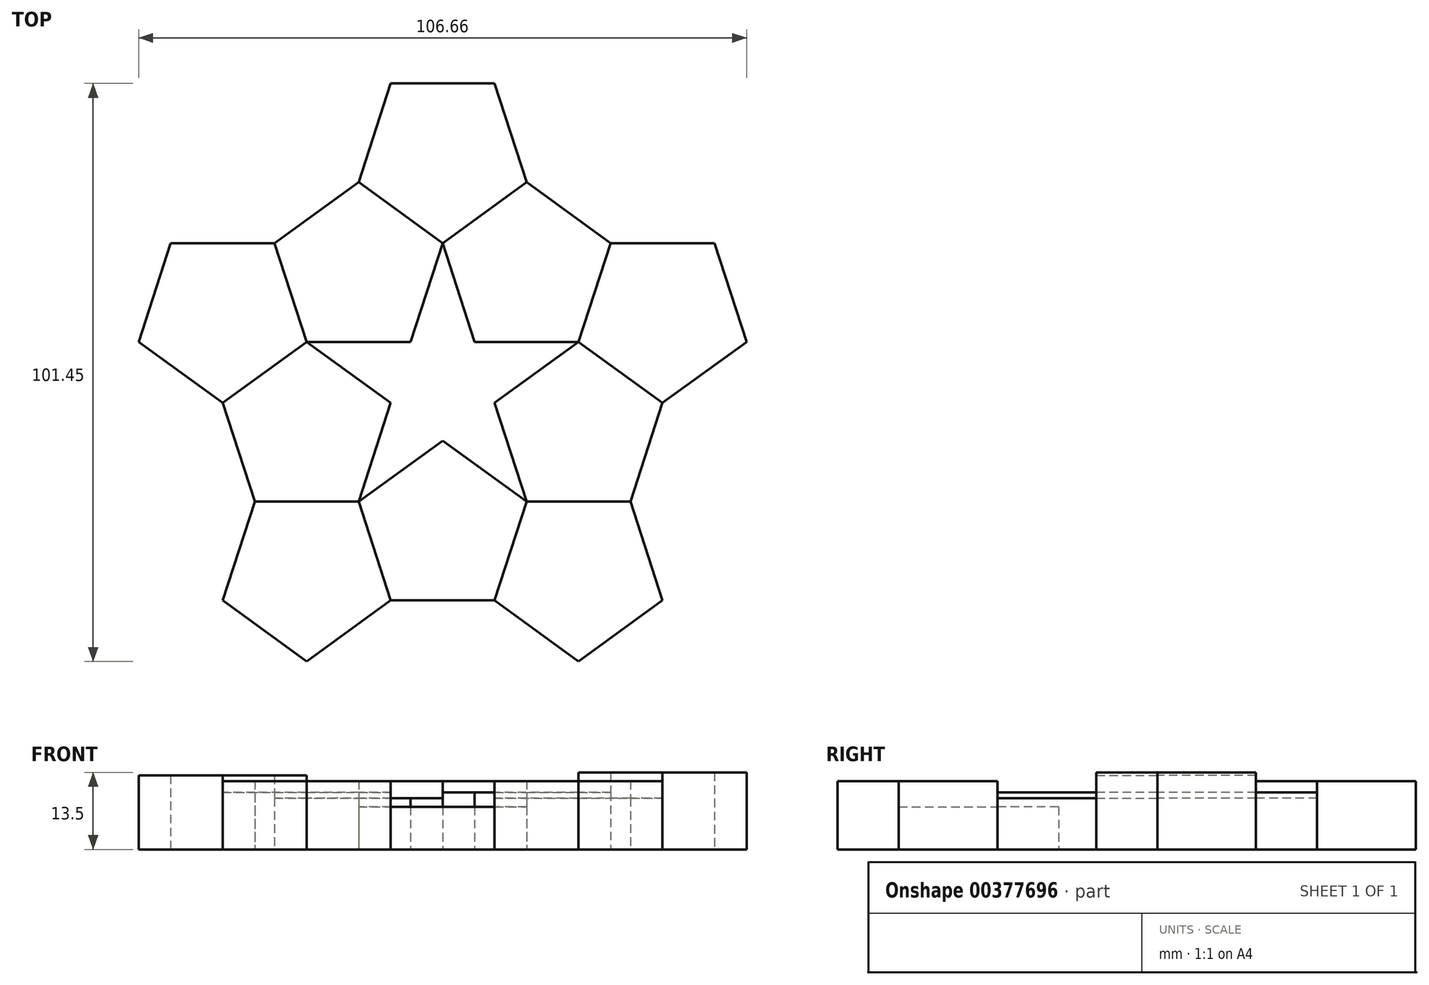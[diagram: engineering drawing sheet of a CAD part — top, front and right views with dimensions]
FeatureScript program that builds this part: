
annotation { "Feature Type Name" : "Feature", "Feature Type Description" : "" }
export const myFeature = defineFeature(function(context is Context, id is Id, definition is map)
    precondition{}
    {
        {
            var Q0;
            Q0=qCreatedBy(makeId("Top.planeOp"),FACE);
            var sketch = newSketch(context, id + "F0", { "sketchPlane" : qUnion([Q0])});
            skCircle(sketch, "E0.cCircle", {"center": v(0, 0) * mm, "radius": 15.5 * mm, "construction": true});
            skLineSegment(sketch, "E0.0", {"start": v(0, 15.5) * mm, "end": v(14.74, 4.79) * mm});
            skLineSegment(sketch, "E0.1", {"start": v(14.74, 4.79) * mm, "end": v(9.11, -12.54) * mm});
            skLineSegment(sketch, "E0.2", {"start": v(9.11, -12.54) * mm, "end": v(-9.11, -12.54) * mm});
            skLineSegment(sketch, "E0.3", {"start": v(-9.11, -12.54) * mm, "end": v(-14.74, 4.79) * mm});
            skLineSegment(sketch, "E0.4", {"start": v(-14.74, 4.79) * mm, "end": v(0, 15.5) * mm});
            skSolve(sketch);
        }
        {
            var Q0;
            Q0=makeQuery(id+"F0.imprint","IMPRINT",FACE,{"disambiguationData":[TD([[makeQuery(id+"F0.imprint","IMPRINT",EDGE,{"derivedFrom":sQuery(id+"F0.wireOp",EDGE,"E0.0")}),-1.0]])]});
            extrude(context, id + "F1", {"entities" : qUnion([Q0]), "depth" : 7.5 * mm});
        }
        {
            var Q0;
            Q0=qCreatedBy(makeId("Top.planeOp"),FACE);
            var sketch = newSketch(context, id + "F2", { "sketchPlane" : qUnion([Q0])});
            skCircle(sketch, "E1.cCircle", {"center": v(23.85, -7.75) * mm, "radius": 15.5 * mm, "construction": true});
            skLineSegment(sketch, "E1.0", {"start": v(14.74, 4.79) * mm, "end": v(32.96, 4.79) * mm});
            skLineSegment(sketch, "E1.1", {"start": v(32.96, 4.79) * mm, "end": v(38.6, -12.54) * mm});
            skLineSegment(sketch, "E1.2", {"start": v(38.6, -12.54) * mm, "end": v(23.85, -23.25) * mm});
            skLineSegment(sketch, "E1.3", {"start": v(23.85, -23.25) * mm, "end": v(9.11, -12.54) * mm});
            skLineSegment(sketch, "E1.4", {"start": v(9.11, -12.54) * mm, "end": v(14.74, 4.79) * mm});
            skSolve(sketch);
        }
        {
            var Q0;
            Q0 = qSketchRegion(id + "F2", true);
            extrude(context, id + "F3", {"entities" : qUnion([Q0]), "operationType" : NewBodyOperationType.ADD, "depth" : 12 * mm});
        }
        {
            var Q0;
            Q0=qCreatedBy(makeId("Top.planeOp"),FACE);
            var sketch = newSketch(context, id + "F4", { "sketchPlane" : qUnion([Q0])});
            skCircle(sketch, "E2.cCircle", {"center": v(23.85, 17.33) * mm, "radius": 15.5 * mm, "construction": true});
            skLineSegment(sketch, "E2.0", {"start": v(32.96, 4.79) * mm, "end": v(14.74, 4.79) * mm});
            skLineSegment(sketch, "E2.1", {"start": v(14.74, 4.79) * mm, "end": v(9.11, 22.12) * mm});
            skLineSegment(sketch, "E2.2", {"start": v(9.11, 22.12) * mm, "end": v(23.85, 32.83) * mm});
            skLineSegment(sketch, "E2.3", {"start": v(23.85, 32.83) * mm, "end": v(38.6, 22.12) * mm});
            skLineSegment(sketch, "E2.4", {"start": v(38.6, 22.12) * mm, "end": v(32.96, 4.79) * mm});
            skSolve(sketch);
        }
        {
            var Q0;
            Q0=makeQuery(id+"F4.imprint","IMPRINT",FACE,{"disambiguationData":[TD([[makeQuery(id+"F4.imprint","IMPRINT",EDGE,{"derivedFrom":sQuery(id+"F4.wireOp",EDGE,"E2.0")}),-1.0]])]});
            extrude(context, id + "F5", {"entities" : qUnion([Q0]), "operationType" : NewBodyOperationType.ADD, "depth" : 9 * mm});
        }
        {
            var Q0;
            Q0=qCreatedBy(makeId("Top.planeOp"),FACE);
            var sketch = newSketch(context, id + "F6", { "sketchPlane" : qUnion([Q0])});
            skCircle(sketch, "E3.cCircle", {"center": v(38.6, 37.62) * mm, "radius": 15.5 * mm, "construction": true});
            skLineSegment(sketch, "E3.0", {"start": v(38.6, 22.12) * mm, "end": v(23.85, 32.83) * mm});
            skLineSegment(sketch, "E3.1", {"start": v(23.85, 32.83) * mm, "end": v(29.48, 50.16) * mm});
            skLineSegment(sketch, "E3.2", {"start": v(29.48, 50.16) * mm, "end": v(47.7, 50.16) * mm});
            skLineSegment(sketch, "E3.3", {"start": v(47.7, 50.16) * mm, "end": v(53.33, 32.83) * mm});
            skLineSegment(sketch, "E3.4", {"start": v(53.33, 32.83) * mm, "end": v(38.6, 22.12) * mm});
            skSolve(sketch);
        }
        {
            var Q0;
            Q0=makeQuery(id+"F6.imprint","IMPRINT",FACE,{"disambiguationData":[TD([[makeQuery(id+"F6.imprint","IMPRINT",EDGE,{"derivedFrom":sQuery(id+"F6.wireOp",EDGE,"E3.0")}),-1.0]])]});
            extrude(context, id + "F7", {"entities" : qUnion([Q0]), "operationType" : NewBodyOperationType.ADD, "depth" : 13.5 * mm});
        }
        {
            var Q0;
            Q0=qCreatedBy(makeId("Top.planeOp"),FACE);
            var sketch = newSketch(context, id + "F8", { "sketchPlane" : qUnion([Q0])});
            skCircle(sketch, "E4.cCircle", {"center": v(14.74, 45.37) * mm, "radius": 15.5 * mm, "construction": true});
            skLineSegment(sketch, "E4.0", {"start": v(23.85, 32.83) * mm, "end": v(5.63, 32.83) * mm});
            skLineSegment(sketch, "E4.1", {"start": v(5.63, 32.83) * mm, "end": v(0, 50.16) * mm});
            skLineSegment(sketch, "E4.2", {"start": v(0, 50.16) * mm, "end": v(14.74, 60.87) * mm});
            skLineSegment(sketch, "E4.3", {"start": v(14.74, 60.87) * mm, "end": v(29.48, 50.16) * mm});
            skLineSegment(sketch, "E4.4", {"start": v(29.48, 50.16) * mm, "end": v(23.85, 32.83) * mm});
            skSolve(sketch);
        }
        {
            var Q0;
            Q0=makeQuery(id+"F8.imprint","IMPRINT",FACE,{"disambiguationData":[TD([[makeQuery(id+"F8.imprint","IMPRINT",EDGE,{"derivedFrom":sQuery(id+"F8.wireOp",EDGE,"E4.0")}),-1.0]])]});
            extrude(context, id + "F9", {"entities" : qUnion([Q0]), "operationType" : NewBodyOperationType.ADD, "depth" : 10 * mm});
        }
        {
            var Q0;
            Q0=qCreatedBy(makeId("Top.planeOp"),FACE);
            var sketch = newSketch(context, id + "F10", { "sketchPlane" : qUnion([Q0])});
            skCircle(sketch, "E5.cCircle", {"center": v(0, 65.66) * mm, "radius": 15.5 * mm, "construction": true});
            skLineSegment(sketch, "E5.0", {"start": v(0, 50.16) * mm, "end": v(-14.74, 60.87) * mm});
            skLineSegment(sketch, "E5.1", {"start": v(-14.74, 60.87) * mm, "end": v(-9.11, 78.2) * mm});
            skLineSegment(sketch, "E5.2", {"start": v(-9.11, 78.2) * mm, "end": v(9.11, 78.2) * mm});
            skLineSegment(sketch, "E5.3", {"start": v(9.11, 78.2) * mm, "end": v(14.74, 60.87) * mm});
            skLineSegment(sketch, "E5.4", {"start": v(14.74, 60.87) * mm, "end": v(0, 50.16) * mm});
            skSolve(sketch);
        }
        {
            var Q0;
            Q0=makeQuery(id+"F10.imprint","IMPRINT",FACE,{"disambiguationData":[TD([[makeQuery(id+"F10.imprint","IMPRINT",EDGE,{"derivedFrom":sQuery(id+"F10.wireOp",EDGE,"E5.0")}),-1.0]])]});
            extrude(context, id + "F11", {"entities" : qUnion([Q0]), "operationType" : NewBodyOperationType.ADD, "depth" : 12 * mm});
        }
        {
            var Q0;
            Q0=qCreatedBy(makeId("Top.planeOp"),FACE);
            var sketch = newSketch(context, id + "F12", { "sketchPlane" : qUnion([Q0])});
            skCircle(sketch, "E6.cCircle", {"center": v(-14.74, 45.37) * mm, "radius": 15.5 * mm, "construction": true});
            skLineSegment(sketch, "E6.0", {"start": v(-5.63, 32.83) * mm, "end": v(-23.85, 32.83) * mm});
            skLineSegment(sketch, "E6.1", {"start": v(-23.85, 32.83) * mm, "end": v(-29.48, 50.16) * mm});
            skLineSegment(sketch, "E6.2", {"start": v(-29.48, 50.16) * mm, "end": v(-14.74, 60.87) * mm});
            skLineSegment(sketch, "E6.3", {"start": v(-14.74, 60.87) * mm, "end": v(0, 50.16) * mm});
            skLineSegment(sketch, "E6.4", {"start": v(0, 50.16) * mm, "end": v(-5.63, 32.83) * mm});
            skSolve(sketch);
        }
        {
            var Q0;
            Q0=makeQuery(id+"F12.imprint","IMPRINT",FACE,{"disambiguationData":[TD([[makeQuery(id+"F12.imprint","IMPRINT",EDGE,{"derivedFrom":sQuery(id+"F12.wireOp",EDGE,"E6.0")}),-1.0]])]});
            extrude(context, id + "F13", {"entities" : qUnion([Q0]), "operationType" : NewBodyOperationType.ADD, "depth" : 9 * mm});
        }
        {
            var Q0;
            Q0=qCreatedBy(makeId("Top.planeOp"),FACE);
            var sketch = newSketch(context, id + "F14", { "sketchPlane" : qUnion([Q0])});
            skCircle(sketch, "E7.cCircle", {"center": v(-38.6, 37.62) * mm, "radius": 15.5 * mm, "construction": true});
            skLineSegment(sketch, "E7.0", {"start": v(-38.6, 22.12) * mm, "end": v(-53.33, 32.83) * mm});
            skLineSegment(sketch, "E7.1", {"start": v(-53.33, 32.83) * mm, "end": v(-47.7, 50.16) * mm});
            skLineSegment(sketch, "E7.2", {"start": v(-47.7, 50.16) * mm, "end": v(-29.48, 50.16) * mm});
            skLineSegment(sketch, "E7.3", {"start": v(-29.48, 50.16) * mm, "end": v(-23.85, 32.83) * mm});
            skLineSegment(sketch, "E7.4", {"start": v(-23.85, 32.83) * mm, "end": v(-38.6, 22.12) * mm});
            skSolve(sketch);
        }
        {
            var Q0;
            Q0=makeQuery(id+"F14.imprint","IMPRINT",FACE,{"disambiguationData":[TD([[makeQuery(id+"F14.imprint","IMPRINT",EDGE,{"derivedFrom":sQuery(id+"F14.wireOp",EDGE,"E7.0")}),-1.0]])]});
            extrude(context, id + "F15", {"entities" : qUnion([Q0]), "operationType" : NewBodyOperationType.ADD, "depth" : 13 * mm});
        }
        {
            var Q0;
            Q0=qCreatedBy(makeId("Top.planeOp"),FACE);
            var sketch = newSketch(context, id + "F16", { "sketchPlane" : qUnion([Q0])});
            skCircle(sketch, "E8.cCircle", {"center": v(-23.85, 17.33) * mm, "radius": 15.5 * mm, "construction": true});
            skLineSegment(sketch, "E8.0", {"start": v(-14.74, 4.79) * mm, "end": v(-32.96, 4.79) * mm});
            skLineSegment(sketch, "E8.1", {"start": v(-32.96, 4.79) * mm, "end": v(-38.6, 22.12) * mm});
            skLineSegment(sketch, "E8.2", {"start": v(-38.6, 22.12) * mm, "end": v(-23.85, 32.83) * mm});
            skLineSegment(sketch, "E8.3", {"start": v(-23.85, 32.83) * mm, "end": v(-9.11, 22.12) * mm});
            skLineSegment(sketch, "E8.4", {"start": v(-9.11, 22.12) * mm, "end": v(-14.74, 4.79) * mm});
            skSolve(sketch);
        }
        {
            var Q0;
            Q0=makeQuery(id+"F16.imprint","IMPRINT",FACE,{"disambiguationData":[TD([[makeQuery(id+"F16.imprint","IMPRINT",EDGE,{"derivedFrom":sQuery(id+"F16.wireOp",EDGE,"E8.0")}),-1.0]])]});
            var Q1;
            Q1=makeQuery(id+"F15.opExtrude","CAP_FACE",FACE,{"disambiguationData":[OSD([sQuery(id+"F14.wireOp",EDGE,"E7.0"),sQuery(id+"F14.wireOp",EDGE,"E7.1"),sQuery(id+"F14.wireOp",EDGE,"E7.2"),sQuery(id+"F14.wireOp",EDGE,"E7.3"),sQuery(id+"F14.wireOp",EDGE,"E7.4")])],"isStart":false});
            extrude(context, id + "F17", {"entities" : qUnion([Q0]), "endBoundEntityFace" : qUnion([Q1]), "depth" : 10 * mm});
        }
        {
            var Q0;
            Q0=qCreatedBy(makeId("Top.planeOp"),FACE);
            var sketch = newSketch(context, id + "F18", { "sketchPlane" : qUnion([Q0])});
            skCircle(sketch, "E9.cCircle", {"center": v(-23.85, -7.75) * mm, "radius": 15.5 * mm, "construction": true});
            skLineSegment(sketch, "E9.0", {"start": v(-9.11, -12.54) * mm, "end": v(-23.85, -23.25) * mm});
            skLineSegment(sketch, "E9.1", {"start": v(-23.85, -23.25) * mm, "end": v(-38.6, -12.54) * mm});
            skLineSegment(sketch, "E9.2", {"start": v(-38.6, -12.54) * mm, "end": v(-32.96, 4.79) * mm});
            skLineSegment(sketch, "E9.3", {"start": v(-32.96, 4.79) * mm, "end": v(-14.74, 4.79) * mm});
            skLineSegment(sketch, "E9.4", {"start": v(-14.74, 4.79) * mm, "end": v(-9.11, -12.54) * mm});
            skSolve(sketch);
        }
        {
            var Q0;
            Q0 = qSketchRegion(id + "F18", true);
            var Q1;
            Q1=makeQuery(id+"F18.imprint","IMPRINT",FACE,{"disambiguationData":[TD([[makeQuery(id+"F18.imprint","IMPRINT",EDGE,{"derivedFrom":sQuery(id+"F18.wireOp",EDGE,"E9.0")}),-1.0]])]});
            extrude(context, id + "F19", {"entities" : qUnion([Q0, Q1]), "depth" : 12 * mm});
        }
    });
